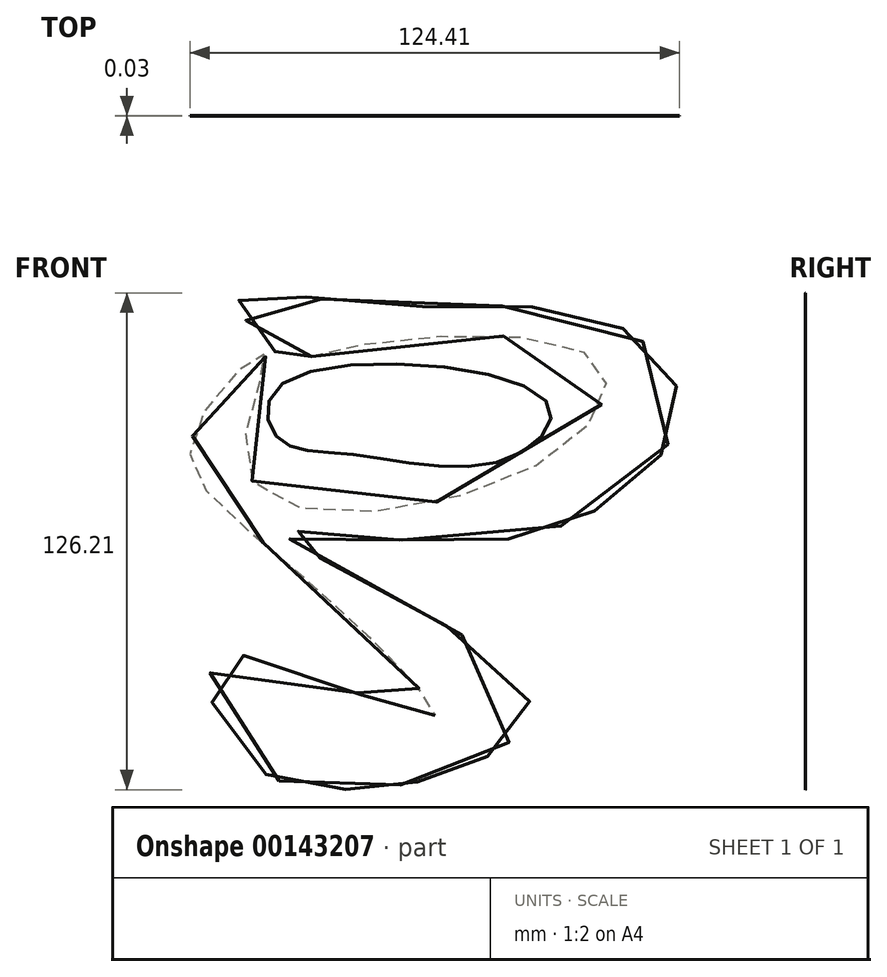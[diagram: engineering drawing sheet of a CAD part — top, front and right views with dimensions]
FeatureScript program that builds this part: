
annotation { "Feature Type Name" : "Feature", "Feature Type Description" : "" }
export const myFeature = defineFeature(function(context is Context, id is Id, definition is map)
    precondition{}
    {
        {
            var Q0;
            Q0=qCreatedBy(makeId("Front.planeOp"),FACE);
            var sketch = newSketch(context, id + "F0", { "sketchPlane" : qUnion([Q0])});
            skFitSpline(sketch, "E0", {"points": [v(-40.38, 37.8) * mm, v(30.67, 37.8) * mm, v(19.13, 11.39) * mm, v(-56.17, 7.44) * mm, v(-52.23, 38.1) * mm, v(-70.45, 18.07) * mm, v(-50.1, -11.7) * mm, v(-9.72, -54.2) * mm, v(-62.85, -38.71) * mm, v(-56.78, -64.83) * mm, v(-25.2, -71.81) * mm, v(0, -66.04) * mm, v(14.27, -47.52) * mm, v(-46.46, -8.05) * mm, v(-12.15, -9.26) * mm, v(34, 0) * mm, v(53.14, 25.35) * mm, v(33.7, 47.22) * mm, v(-23.99, 50.86) * mm, v(-58.9, 51.47) * mm, v(-45.85, 36.29) * mm, v(-40.38, 37.8) * mm]});
            skSolve(sketch);
        }
        {
            var Q0;
            Q0=makeQuery(id+"F0.imprint","IMPRINT",FACE,{"disambiguationData":[TD([[makeQuery(id+"F0.imprint","IMPRINT",EDGE,{"derivedFrom":sQuery(id+"F0.wireOp",EDGE,"E0")}),1.0]])]});
            extrude(context, id + "F1", {"entities" : qUnion([Q0]), "depth" : 0.03 * mm});
        }
        {
            var Q0;
            Q0=qCreatedBy(makeId("Front.planeOp"),FACE);
            var sketch = newSketch(context, id + "F2", { "sketchPlane" : qUnion([Q0])});
            skFitSpline(sketch, "E1", {"points": [v(-47.77, 30.85) * mm, v(-48.68, 16.87) * mm, v(-30.14, 12.92) * mm, v(8.46, 11.4) * mm, v(19.4, 26.3) * mm, v(-47.77, 30.85) * mm]});
            skSolve(sketch);
        }
        {
            var Q0;
            Q0=makeQuery(id+"F2.imprint","IMPRINT",FACE,{"disambiguationData":[TD([[makeQuery(id+"F2.imprint","IMPRINT",EDGE,{"derivedFrom":sQuery(id+"F2.wireOp",EDGE,"E1")}),1.0]])]});
            extrude(context, id + "F3", {"entities" : qUnion([Q0]), "depth" : 0.03 * mm});
        }
    });
